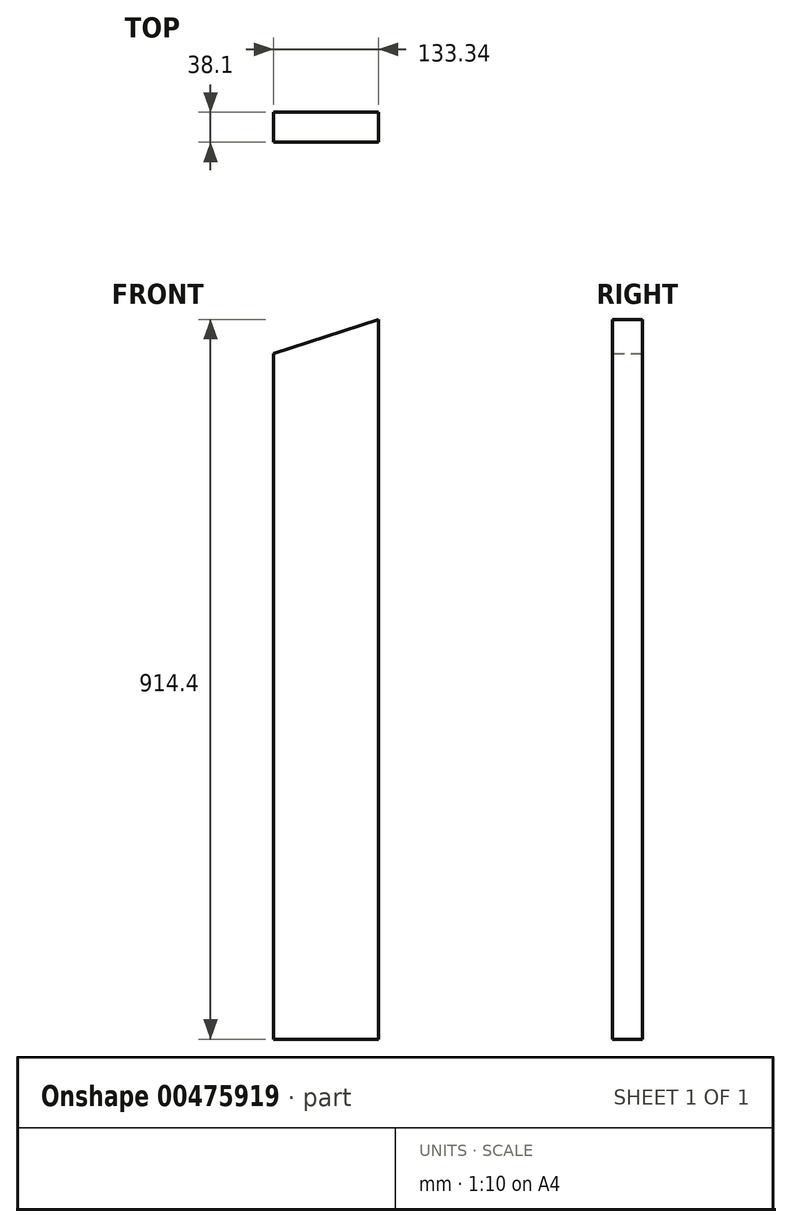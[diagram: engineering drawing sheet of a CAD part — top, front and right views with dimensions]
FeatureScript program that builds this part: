
annotation { "Feature Type Name" : "Feature", "Feature Type Description" : "" }
export const myFeature = defineFeature(function(context is Context, id is Id, definition is map)
    precondition{}
    {
        {
            var Q0;
            Q0=qCreatedBy(makeId("Front.planeOp"),FACE);
            var sketch = newSketch(context, id + "F0", { "sketchPlane" : qUnion([Q0])});
            skLineSegment(sketch, "E0.top", {"start": v(66.68, -457.2) * mm, "end": v(-66.68, -457.2) * mm});
            skLineSegment(sketch, "E0.left", {"start": v(66.68, 457.2) * mm, "end": v(66.67, -457.2) * mm});
            skLineSegment(sketch, "E0.right", {"start": v(-66.67, 413.88) * mm, "end": v(-66.68, -457.2) * mm});
            skPoint(sketch, "E0.middle", {"position": v(0, 0) * mm});
            skLineSegment(sketch, "E1", {"start": v(66.68, 457.2) * mm, "end": v(-66.67, 413.88) * mm});
            skSolve(sketch);
        }
        {
            var Q0;
            Q0=qSketchRegion(id+"F0",true);
            extrude(context, id + "F1", {"entities" : qUnion([Q0]), "endBound" : BoundingType.SYMMETRIC, "depth" : 38.1 * mm, "offsetDistance" : 25.4 * mm});
        }
    });
